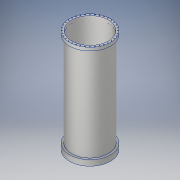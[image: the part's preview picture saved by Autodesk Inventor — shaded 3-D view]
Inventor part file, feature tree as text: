
AUTODESK INVENTOR PART (.ipt)
format: ipt  version: 2018 (Build 220112000, 112)  size: 172,544 bytes
history: native  units: in
note: dims shown in document units (in); Inventor stores cm internally (conversion verified against a paired STEP export)
features: sketch x5, extrude x4, hole x1, pattern_circular x1
ambient origin geometry x8: Origin, YZ Plane, XZ Plane, XY Plane, X Axis, Y Axis, Z Axis, Center Point
bodies: Solid1 (feature_tree)
feature tree (11):
  extrude  "Extrusion1"  Depth=11.375in
  extrude  "Extrusion2"  Depth=1.0in
  extrude  "Extrusion3"  Depth=29.25in TaperAngle=0.0deg
  extrude  "Extrusion4"  Depth=12.75in
  hole  "Hole1"  [1 undecoded]
  pattern_circular  "Circular Pattern1"  [2 undecoded]
  sketch  "Sketch1"  dims[d0=12.75in d1=11.375in]
  sketch  "Sketch2"  dims[d2=1.0in d3=0.0in d4=11.375in]
  sketch  "Sketch3"  dims[d5=11.5in d6=29.25in d7=0.0in]
  sketch  "Sketch4"  dims[d8=11.375in d9=12.75in]
  sketch  "Sketch5"  dims[d10=1.0in d11=0.0in d12=12.75in d13=0.75in d14=0.0in d15=6.125in d16=0.0344in d17=0.266in d18=0.472in d19=0.375in d20=0.25in d21=0.5635in d22=0.673in d23=0.8108in d24=14.1732in d25=360.0deg]
note: 3 required parameter values undecoded (feature->parameter linkage not recoverable at this tier; creation-order binding heuristic only, values carry confidence <= 0.55)
